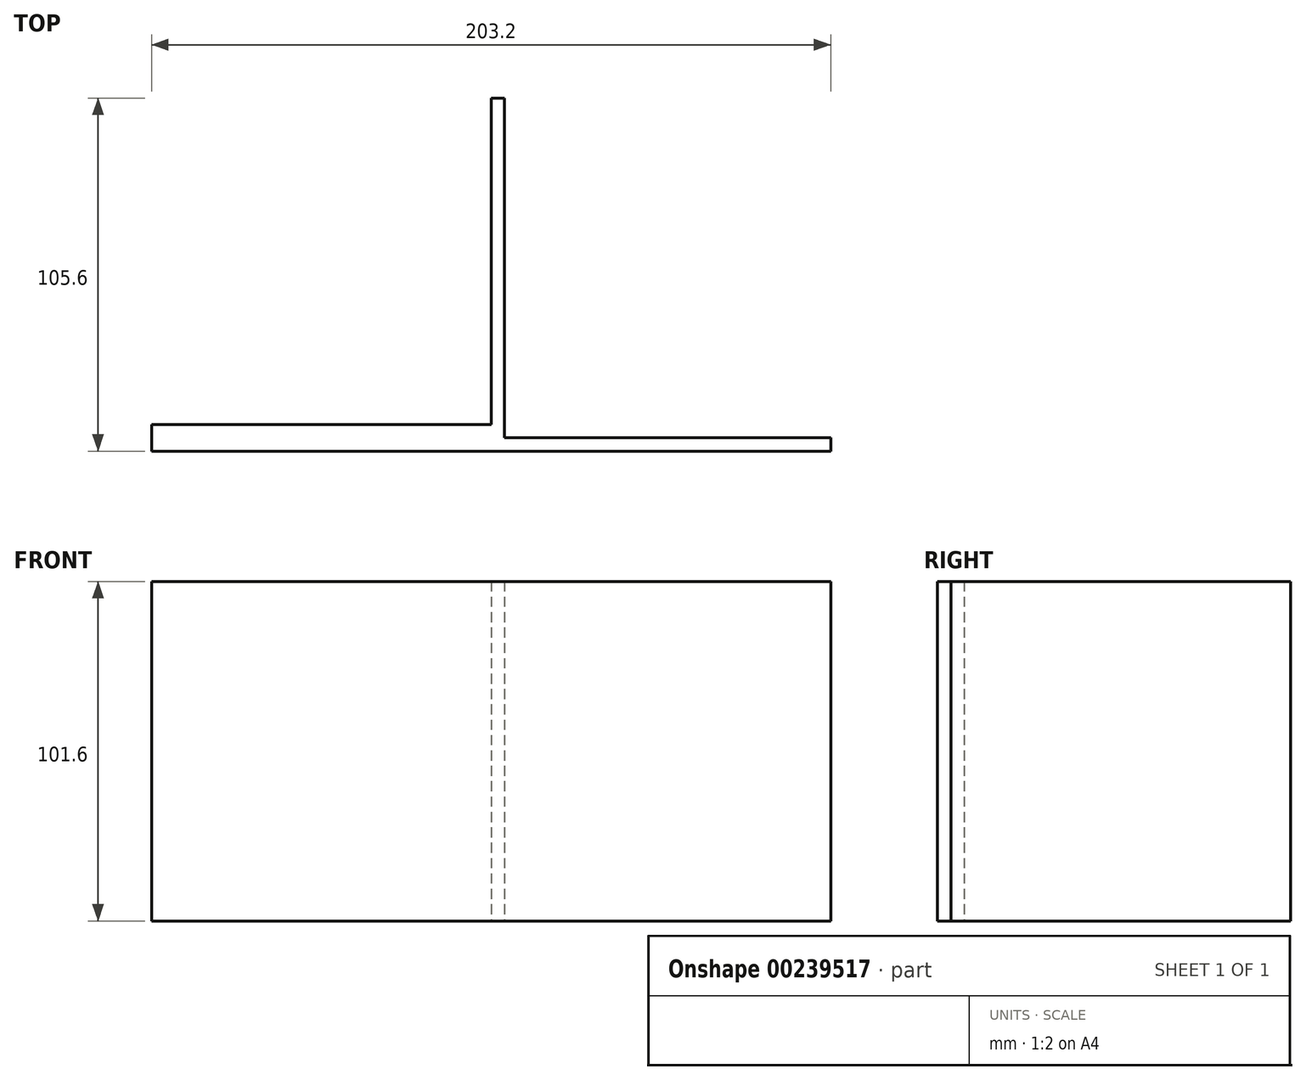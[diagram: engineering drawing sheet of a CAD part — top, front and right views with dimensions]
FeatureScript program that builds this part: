
annotation { "Feature Type Name" : "Feature", "Feature Type Description" : "" }
export const myFeature = defineFeature(function(context is Context, id is Id, definition is map)
    precondition{}
    {
        {
            assignVariable(context, id + "F0", {"name" : "P", "anyValue" : 4});
        }
        {
            var Q0;
            Q0=qCreatedBy(makeId("Front.planeOp"),FACE);
            var sketch = newSketch(context, id + "F1", { "sketchPlane" : qUnion([Q0])});
            skLineSegment(sketch, "E0.bottom", {"start": v(-50.8, 50.8) * mm, "end": v(50.8, 50.8) * mm});
            skLineSegment(sketch, "E0.top", {"start": v(-50.8, -50.8) * mm, "end": v(50.8, -50.8) * mm});
            skLineSegment(sketch, "E0.left", {"start": v(-50.8, 50.8) * mm, "end": v(-50.8, -50.8) * mm});
            skLineSegment(sketch, "E0.right", {"start": v(50.8, 50.8) * mm, "end": v(50.8, -50.8) * mm});
            skPoint(sketch, "E0.middle", {"position": v(0, 0) * mm});
            skSolve(sketch);
        }
        {
            var Q0;
            Q0 = qSketchRegion(id + "F1", true);
            extrude(context, id + "F2", {"entities" : qUnion([Q0]), "endBound" : BoundingType.SYMMETRIC, "depth" : ((getVariable(context, 'P')) * (2)) * mm});
        }
        {
            var Q0;
            Q0=makeQuery(id+"F2.opExtrude","SWEPT_FACE",FACE,{"disambiguationData":[OSD([sQuery(id+"F1.wireOp",EDGE,"E0.right")])]});
            var sketch = newSketch(context, id + "F3", { "sketchPlane" : qUnion([Q0])});
            skLineSegment(sketch, "E1.bottom", {"start": v(101.6, 50.8) * mm, "end": v(0, 50.8) * mm});
            skLineSegment(sketch, "E1.top", {"start": v(101.6, -50.8) * mm, "end": v(0, -50.8) * mm});
            skLineSegment(sketch, "E1.left", {"start": v(101.6, 50.8) * mm, "end": v(101.6, -50.8) * mm});
            skLineSegment(sketch, "E1.right", {"start": v(0, 50.8) * mm, "end": v(0, -50.8) * mm});
            skSolve(sketch);
        }
        {
            var Q0;
            Q0 = qSketchRegion(id + "F3", true);
            extrude(context, id + "F4", {"entities" : qUnion([Q0]), "operationType" : NewBodyOperationType.ADD, "depth" : (getVariable(context, 'P')) * mm});
        }
        {
            var Q0;
            Q0=makeQuery(id+"F4.opExtrude","SWEPT_FACE",FACE,{"disambiguationData":[OSD([sQuery(id+"F3.wireOp",EDGE,"E1.right")])]});
            var sketch = newSketch(context, id + "F5", { "sketchPlane" : qUnion([Q0])});
            skLineSegment(sketch, "E2.bottom", {"start": v(152.4, 50.8) * mm, "end": v(50.8, 50.8) * mm});
            skLineSegment(sketch, "E2.top", {"start": v(152.4, -50.8) * mm, "end": v(50.8, -50.8) * mm});
            skLineSegment(sketch, "E2.left", {"start": v(152.4, 50.8) * mm, "end": v(152.4, -50.8) * mm});
            skLineSegment(sketch, "E2.right", {"start": v(50.8, 50.8) * mm, "end": v(50.8, -50.8) * mm});
            skSolve(sketch);
        }
        {
            var Q0;
            Q0 = qSketchRegion(id + "F5", true);
            extrude(context, id + "F6", {"entities" : qUnion([Q0]), "operationType" : NewBodyOperationType.ADD, "depth" : (getVariable(context, 'P')) * mm});
        }
    });
